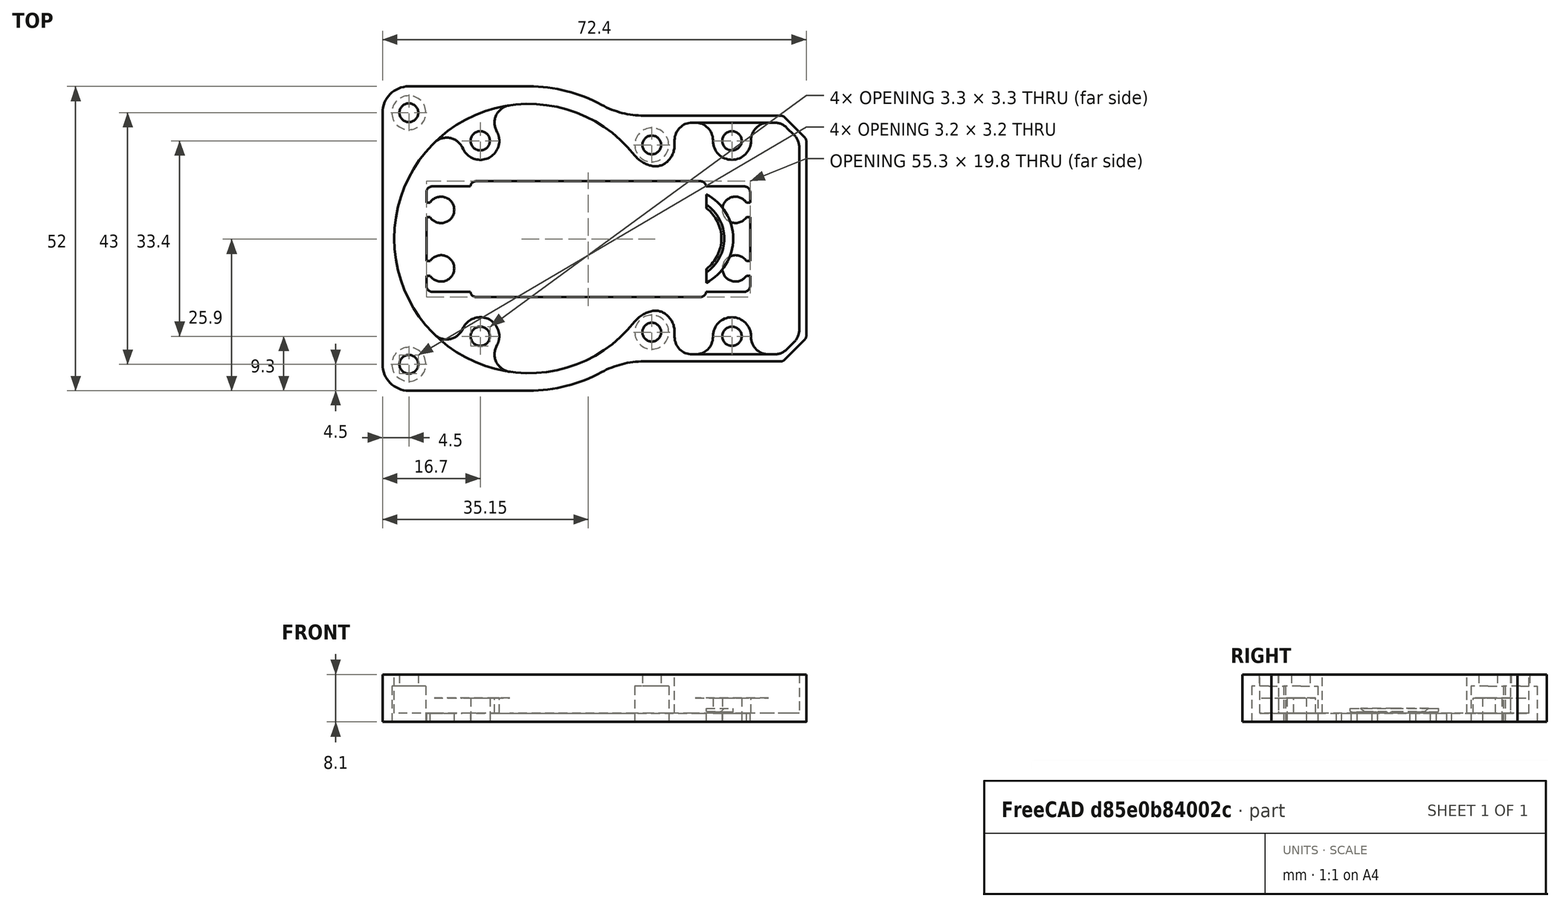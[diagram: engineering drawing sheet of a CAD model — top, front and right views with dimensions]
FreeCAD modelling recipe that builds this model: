
FCSTD DOCUMENT  (FreeCAD 0.18.4R)
Label: motor_part
License: All rights reserved
LicenseURL: http://en.wikipedia.org/wiki/All_rights_reserved
objects: Part::Feature×2, Sketcher::SketchObject×2, Part::FeaturePython×1
note: 5 computed .brp shape members not serialized (recipe doc carries the construction recipe); baked Part::Feature solids carry a one-line shape summary decoded from their .brp

FEATURE [Part::Feature] Part__Feature065  label="motor_support"
  shape: bbox 72.4 x 52 x 8.1 mm, 112 faces (baked)
FEATURE [Part::Feature] Part__Feature006  label="Case"
  Placement = pos=(-10,-10,2) rot=(0.707107,0.707107,0;3.14159rad)
  shape: bbox 68.3 x 20.02 x 42.1 mm, 433 faces (baked)
FEATURE [Part::FeaturePython] Cutout  # WARN: FeaturePython — macro-defined, semantics opaque (R4)
  Base = -> Part__Feature065
  Tolerance = 0
  Tool = -> Part__Feature006
FEATURE [Sketcher::SketchObject] Sketch
  ExternalGeometry = -> [Part__Feature065,Cutout]
  MapMode = 2
  Support = -> [Part__Feature065]
  sketch-geometry (79):
    g0: LineSegment StartX=-20.5 StartY=26 StartZ=0 EndX=-1.07e-14 EndY=26 EndZ=0
    g1: LineSegment StartX=-25 StartY=21.5 StartZ=0 EndX=-25 EndY=-21.5 EndZ=0
    g2: ArcOfCircle CenterX=-20.5 CenterY=-21.5 CenterZ=0 NormalX=0 NormalY=0 NormalZ=1 AngleXU=0 Radius=4.5 StartAngle=3.14159 EndAngle=4.71239
    g3: LineSegment StartX=-20.5 StartY=-26 StartZ=0 EndX=0 EndY=-26 EndZ=0
    g4: ArcOfCircle CenterX=2.88e-14 CenterY=-1.284e-13 CenterZ=0 NormalX=0 NormalY=0 NormalZ=1 AngleXU=0 Radius=26 StartAngle=4.71239 EndAngle=5.21142
    g5: ArcOfCircle CenterX=19.6214 CenterY=-36 CenterZ=0 NormalX=0 NormalY=0 NormalZ=1 AngleXU=0 Radius=15 StartAngle=1.5708 EndAngle=2.06982
    g6: LineSegment StartX=19.6214 StartY=-21 StartZ=0 EndX=42.9858 EndY=-21 EndZ=0
    g7: ArcOfCircle CenterX=42.9858 CenterY=-20 CenterZ=0 NormalX=0 NormalY=0 NormalZ=1 AngleXU=0 Radius=1 StartAngle=4.71239 EndAngle=5.49779
    g8: LineSegment StartX=43.6929 StartY=-20.7071 StartZ=0 EndX=47.1071 EndY=-17.2929 EndZ=0
    g9: LineSegment StartX=47.4 StartY=-16.5858 StartZ=0 EndX=47.4 EndY=16.5858 EndZ=0
    g10: ArcOfCircle CenterX=46.4 CenterY=16.5858 CenterZ=0 NormalX=0 NormalY=0 NormalZ=1 AngleXU=0 Radius=1 StartAngle=0 EndAngle=0.785398
    g11: ArcOfCircle CenterX=8.48e-14 CenterY=3.027e-13 CenterZ=0 NormalX=0 NormalY=0 NormalZ=1 AngleXU=0 Radius=26 StartAngle=1.07177 EndAngle=1.5708
    g12: ArcOfCircle CenterX=-20.5 CenterY=21.5 CenterZ=0 NormalX=0 NormalY=0 NormalZ=1 AngleXU=0 Radius=4.5 StartAngle=1.5708 EndAngle=3.14159
    g13: LineSegment StartX=27.9 StartY=19.8 StartZ=0 EndX=41.9574 EndY=19.8 EndZ=0
    g14: ArcOfCircle CenterX=28.45 CenterY=16.8 CenterZ=0 NormalX=0 NormalY=0 NormalZ=1 AngleXU=0 Radius=3 StartAngle=3e-16 EndAngle=1.5708
    g15: LineSegment StartX=31.45 StartY=16.7 StartZ=0 EndX=31.45 EndY=16.8 EndZ=0
    g16: ArcOfCircle CenterX=34.7 CenterY=16.7 CenterZ=0 NormalX=0 NormalY=0 NormalZ=1 AngleXU=0 Radius=3.25 StartAngle=3.14159 EndAngle=6.28319
    g17: LineSegment StartX=37.95 StartY=16.8 StartZ=0 EndX=37.95 EndY=16.7 EndZ=0
    g18: ArcOfCircle CenterX=40.95 CenterY=16.8 CenterZ=0 NormalX=0 NormalY=0 NormalZ=1 AngleXU=0 Radius=3 StartAngle=1.5708 EndAngle=3.14159
    g19: ArcOfCircle CenterX=41.9574 CenterY=16.8 CenterZ=0 NormalX=0 NormalY=0 NormalZ=1 AngleXU=0 Radius=3 StartAngle=0.785398 EndAngle=1.5708
    g20: LineSegment StartX=44.0789 StartY=18.9211 StartZ=0 EndX=45.3213 EndY=17.6787 EndZ=0
    g21: ArcOfCircle CenterX=43.2 CenterY=15.5574 CenterZ=0 NormalX=0 NormalY=0 NormalZ=1 AngleXU=0 Radius=3 StartAngle=0 EndAngle=0.785398
    g22: LineSegment StartX=46.2 StartY=15.5574 StartZ=0 EndX=46.2 EndY=8.9 EndZ=0
    g23: LineSegment StartX=37.95 StartY=-16.8 StartZ=0 EndX=37.95 EndY=-16.7 EndZ=0
    g24: ArcOfCircle CenterX=34.7 CenterY=-16.7 CenterZ=0 NormalX=0 NormalY=0 NormalZ=1 AngleXU=0 Radius=3.25 StartAngle=2e-16 EndAngle=3.14159
    g25: LineSegment StartX=31.45 StartY=-16.8 StartZ=0 EndX=31.45 EndY=-16.7 EndZ=0
    g26: ArcOfCircle CenterX=28.45 CenterY=-16.8 CenterZ=0 NormalX=0 NormalY=0 NormalZ=1 AngleXU=0 Radius=3 StartAngle=4.71239 EndAngle=6.28319
    g27: Circle CenterX=34.7 CenterY=-16.7 CenterZ=0 NormalX=0 NormalY=0 NormalZ=1 AngleXU=0 Radius=1.65
    g28: ArcOfCircle CenterX=40.95 CenterY=-16.8 CenterZ=0 NormalX=0 NormalY=0 NormalZ=1 AngleXU=0 Radius=3 StartAngle=3.14159 EndAngle=4.71239
    g29: LineSegment StartX=41.9574 StartY=-19.8 StartZ=0 EndX=27.9 EndY=-19.8 EndZ=0
    g30: ArcOfCircle CenterX=41.9574 CenterY=-16.8 CenterZ=0 NormalX=0 NormalY=0 NormalZ=1 AngleXU=0 Radius=3 StartAngle=4.71239 EndAngle=5.49779
    g31: LineSegment StartX=44.0787 StartY=-18.9213 StartZ=0 EndX=45.3213 EndY=-17.6787 EndZ=0
    g32: ArcOfCircle CenterX=43.2 CenterY=-15.5574 CenterZ=0 NormalX=0 NormalY=0 NormalZ=1 AngleXU=0 Radius=3 StartAngle=5.49779 EndAngle=6.28319
    g33: Circle CenterX=34.7 CenterY=16.7 CenterZ=0 NormalX=0 NormalY=0 NormalZ=1 AngleXU=0 Radius=1.65
    g34: LineSegment [constr] StartX=31.45 StartY=16.7 StartZ=0 EndX=33.05 EndY=16.7 EndZ=0
    g35: ArcOfCircle CenterX=19.6214 CenterY=36 CenterZ=0 NormalX=0 NormalY=0 NormalZ=1 AngleXU=0 Radius=15 StartAngle=4.21336 EndAngle=4.71239
    g36: LineSegment StartX=19.6214 StartY=21 StartZ=0 EndX=42.9858 EndY=21 EndZ=0
    g37: ArcOfCircle CenterX=42.9858 CenterY=20 CenterZ=0 NormalX=0 NormalY=0 NormalZ=1 AngleXU=0 Radius=1 StartAngle=0.785398 EndAngle=1.5708
    g38: LineSegment StartX=43.6929 StartY=20.7071 StartZ=0 EndX=47.1068 EndY=17.2932 EndZ=0
    g39: LineSegment [constr] StartX=36.35 StartY=16.7 StartZ=0 EndX=37.95 EndY=16.7 EndZ=0
    g40: LineSegment [constr] StartX=31.45 StartY=-16.7 StartZ=0 EndX=33.05 EndY=-16.7 EndZ=0
    g41: ArcOfCircle CenterX=46.4 CenterY=-16.5858 CenterZ=0 NormalX=0 NormalY=0 NormalZ=1 AngleXU=0 Radius=1 StartAngle=5.49779 EndAngle=6.28319
    g42: ArcOfCircle CenterX=-8.3 CenterY=-16.7 CenterZ=0 NormalX=0 NormalY=0 NormalZ=1 AngleXU=0 Radius=3.25 StartAngle=5.82194 EndAngle=6.28319
    g43: ArcOfCircle CenterX=-8.3 CenterY=-16.7 CenterZ=0 NormalX=0 NormalY=0 NormalZ=1 AngleXU=0 Radius=3.25 StartAngle=-1.42e-14 EndAngle=2.68034
    g44: LineSegment StartX=-11.3659 StartY=-15.5665 StartZ=0 EndX=-11.2104 EndY=-15.2535 EndZ=0
    g45: ArcOfCircle CenterX=-14.0524 CenterY=-14.2313 CenterZ=0 NormalX=0 NormalY=0 NormalZ=1 AngleXU=0 Radius=3 StartAngle=3.93332 EndAngle=5.82194
    g46: LineSegment StartX=-5.54518 StartY=-18.4594 StartZ=0 EndX=-5.38963 EndY=-18.1465 EndZ=0
    g47: ArcOfCircle CenterX=-2.85869 CenterY=-19.7946 CenterZ=0 NormalX=0 NormalY=0 NormalZ=1 AngleXU=0 Radius=3 StartAngle=2.68034 EndAngle=4.56896
    g48: Circle CenterX=-8.3 CenterY=-16.7 CenterZ=0 NormalX=0 NormalY=0 NormalZ=1 AngleXU=0 Radius=1.65
    g49: LineSegment [constr] StartX=-11.3659 StartY=-15.5665 StartZ=0 EndX=-9.89959 EndY=-16.2953 EndZ=0
    g50: ArcOfCircle CenterX=-5.349e-13 CenterY=-1.0646e-12 CenterZ=0 NormalX=0 NormalY=0 NormalZ=1 AngleXU=0 Radius=23 StartAngle=3.93332 EndAngle=4.56896
    g51: LineSegment StartX=27.9 StartY=-19.8 StartZ=0 EndX=19.6214 EndY=-19.8 EndZ=0
    g52: LineSegment [constr] StartX=19.6214 StartY=-21 StartZ=0 EndX=19.6214 EndY=-19.8 EndZ=0
    g53: LineSegment [constr] StartX=12.4428 StartY=-22.8293 StartZ=0 EndX=11.5027 EndY=-21.1043 EndZ=0
    g54: ArcOfCircle CenterX=19.6214 CenterY=-45.7194 CenterZ=0 NormalX=0 NormalY=0 NormalZ=1 AngleXU=0 Radius=25.9194 StartAngle=1.5708 EndAngle=1.88939
    g55: ArcOfCircle CenterX=0.153739 CenterY=13.3044 CenterZ=0 NormalX=0 NormalY=0 NormalZ=1 AngleXU=0 Radius=36.232 StartAngle=4.61727 EndAngle=5.03098
    g56: LineSegment [constr] StartX=-5.38963 StartY=-18.1465 StartZ=0 EndX=-6.82243 EndY=-17.4344 EndZ=0
    g57: LineSegment [constr] StartX=-6.65 StartY=-16.7 StartZ=0 EndX=-5.05 EndY=-16.7 EndZ=0
    g58: ArcOfCircle CenterX=1.28979 CenterY=-14.0146 CenterZ=0 NormalX=0 NormalY=0 NormalZ=1 AngleXU=0 Radius=36.974 StartAngle=1.2522 EndAngle=1.66592
    g59: ArcOfCircle CenterX=-0.0432141 CenterY=-0.043072 CenterZ=0 NormalX=0 NormalY=0 NormalZ=1 AngleXU=0 Radius=22.939 StartAngle=1.66592 EndAngle=2.74111
    g60: ArcOfCircle CenterX=20.955 CenterY=45.608 CenterZ=0 NormalX=0 NormalY=0 NormalZ=1 AngleXU=0 Radius=25.808 StartAngle=4.3938 EndAngle=4.71239
    g61: LineSegment StartX=20.955 StartY=19.8 StartZ=0 EndX=27.9 EndY=19.8 EndZ=0
    g62: Circle CenterX=0 CenterY=2.45e-14 CenterZ=0 NormalX=0 NormalY=0 NormalZ=1 AngleXU=0 Radius=5
    g63: Circle CenterX=-14.9671 CenterY=-5.1 CenterZ=0 NormalX=0 NormalY=0 NormalZ=1 AngleXU=0 Radius=1.9
    g64: LineSegment StartX=-10.9671 StartY=-9.1 StartZ=0 EndX=-21.1185 EndY=-9.1 EndZ=0
    g65: LineSegment StartX=-10.9671 StartY=-9.1 StartZ=0 EndX=-10.9671 EndY=8.9 EndZ=0
    g66: LineSegment StartX=-10.9671 StartY=8.9 StartZ=0 EndX=-21.1671 EndY=8.9 EndZ=0
    g67: Circle CenterX=-15 CenterY=4.9 CenterZ=0 NormalX=0 NormalY=0 NormalZ=1 AngleXU=0 Radius=1.9
    g68: LineSegment [constr] StartX=-15 StartY=4.9 StartZ=0 EndX=-15 EndY=8.9 EndZ=0
    g69: LineSegment [constr] StartX=-14.9671 StartY=-5.1 StartZ=0 EndX=-14.9671 EndY=-9.1 EndZ=0
    g70: LineSegment [constr] StartX=-14.9671 StartY=-5.1 StartZ=0 EndX=-10.9671 EndY=-5.1 EndZ=0
    g71: Circle CenterX=35.3 CenterY=4.9 CenterZ=0 NormalX=0 NormalY=0 NormalZ=1 AngleXU=0 Radius=1.9
    g72: Circle CenterX=35.3 CenterY=-5.1 CenterZ=0 NormalX=0 NormalY=0 NormalZ=1 AngleXU=0 Radius=1.9
    g73: LineSegment [constr] StartX=35.3 StartY=-5.1 StartZ=0 EndX=35.3 EndY=-9.1 EndZ=0
    g74: LineSegment StartX=31.3 StartY=-9.1 StartZ=0 EndX=31.3 EndY=8.9 EndZ=0
    g75: LineSegment StartX=31.3 StartY=8.9 StartZ=0 EndX=46.2 EndY=8.9 EndZ=0
    g76: LineSegment StartX=31.3 StartY=-9.1 StartZ=0 EndX=46.2 EndY=-9.1 EndZ=0
    g77: ArcOfCircle CenterX=-0.0432141 CenterY=-0.043072 CenterZ=0 NormalX=0 NormalY=0 NormalZ=1 AngleXU=0 Radius=22.939 StartAngle=3.54747 EndAngle=3.93334
    g78: LineSegment StartX=46.2 StartY=-9.1 StartZ=0 EndX=46.2 EndY=-15.5574 EndZ=0
  constraints (189):
    c: Coincident(g0,g-4)
    c: Coincident(g0,g-20)
    c: Coincident(g2,g-7)
    c: Coincident(g3,g-8)
    c: Coincident(g4,g3)
    c: Coincident(g4,g-9)
    c: Coincident(g5,g-10)
    c: Coincident(g6,g-11)
    c: Coincident(g7,g-12)
    c: Coincident(g8,g-13)
    c: Coincident(g9,g-15)
    c: Coincident(g10,g-16)
    c: Coincident(g11,g0)
    c: Coincident(g11,g-20) = 1.5708
    c: Tangent(g12,g0) = 1.5708
    c: Tangent(g12,g1) = -1.5708
    c: Tangent(g2,g1) = -1.5708
    c: Tangent(g3,g2) = -1.5708
    c: Radius(g12) = 4.5
    c: Angle(g2) = 1.5708
    c: Tangent(g8,g7) = -1.5708
    c: Coincident(g9,g-14) = -1.5708
    c: Coincident(g13,g-26)
    c: Coincident(g13,g-27)
    c: Coincident(g14,g-21)
    c: Coincident(g14,g-23)
    c: Coincident(g15,g-23)
    c: Tangent(g15,g14) = -1.5708
    c: Coincident(g16,g-24)
    c: Tangent(g16,g15) = 1.5708
    c: Coincident(g17,g-25)
    c: Coincident(g18,g-25)
    c: Tangent(g18,g17) = -1.5708
    c: Coincident(g19,g-28)
    c: Tangent(g19,g13) = 1.5708
    c: Coincident(g20,g-29)
    c: Coincident(g21,g-30)
    c: Tangent(g21,g20) = 1.5708
    c: Tangent(g22,g21) = 1.5708
    c: Coincident(g23,g-37)
    c: Coincident(g23,g-36) = 1.5708
    c: Coincident(g24,g-38)
    c: Tangent(g24,g23) = -1.5708
    c: Coincident(g25,g-39)
    c: Coincident(g26,g-39)
    c: Tangent(g26,g25) = -1.5708
    c: PointOnObject(g-41,g27)
    c: PointOnObject(g-41,g27)
    c: Tangent(g27,g-40)
    c: Coincident(g28,g23)
    c: Coincident(g28,g-35)
    c: Tangent(g28,g-35)
    c: Coincident(g29,g-34)
    c: Coincident(g29,g-34)
    c: Coincident(g30,g29)
    c: Coincident(g30,g-33)
    c: Tangent(g30,g-33)
    c: Coincident(g31,g30)
    c: Coincident(g31,g-32)
    c: PointOnObject(g-43,g33)
    c: PointOnObject(g-43,g33)
    c: Radius(g18) = 3
    c: Coincident(g34,g15)
    c: Coincident(g34,g-43)
    c: Perpendicular(g33,g34)
    c: Distance(g20) = 1.757
    c: Coincident(g35,g-19)
    c: Coincident(g36,g-18)
    c: Coincident(g37,g-17)
    c: Tangent(g35,g11) = 1.5708
    c: Tangent(g36,g35) = -1.5708
    c: Coincident(g39,g-43)
    c: Coincident(g39,g16)
    c: Equal(g17,g15)
    c: Tangent(g10,g9) = -1.5708
    c: Tangent(g7,g6)
    c: Coincident(g40,g24)
    c: Coincident(g40,g-41)
    c: Perpendicular(g25,g40)
    c: DistanceY(g25,g25) = 0.1
    c: Angle(g7) = 0.785398
    c: Tangent(g37,g36) = 1.5708
    c: Tangent(g38,g37) = 1.5708
    c: Tangent(g32,g31) = -1.5708
    c: Tangent(g41,g9) = -1.5708
    c: Tangent(g41,g8)
    c: Tangent(g6,g5) = 1.5708
    c: Tangent(g5,g4) = 1.5708
    c: Distance(g38) = 4.828
    c: Angle(g41) = 0.785398
    c: Coincident(g42,g-46)
    c: Coincident(g43,g-48)
    c: Coincident(g44,g-49)
    c: Coincident(g45,g-49)
    c: Coincident(g46,g-45)
    c: Coincident(g47,g46)
    c: Coincident(g47,g-44)
    c: Tangent(g47,g-44)
    c: PointOnObject(g-51,g48)
    c: PointOnObject(g-51,g48)
    c: Tangent(g45,g44) = -1.5708
    c: Tangent(g44,g43) = 1.5708
    c: Coincident(g49,g44)
    c: PointOnObject(g49,g48)
    c: Perpendicular(g44,g49)
    c: Tangent(g46,g42) = -1.5708
    c: Tangent(g43,g42) = -1.5708
    c: Coincident(g50,g47)
    c: Tangent(g50,g45) = -1.5708
    c: Coincident(g51,g29)
    c: Horizontal(g51)
    c: Coincident(g52,g5)
    c: Coincident(g52,g51)
    c: Perpendicular(g51,g52)
    c: Coincident(g53,g4)
    c: Perpendicular(g5,g53)
    c: Coincident(g54,g53)
    c: Tangent(g54,g51) = -1.5708
    c: Tangent(g55,g54) = 1.5708
    c: Angle(g54) = 0.318592
    c: Angle(g55) = 0.413713
    c: Radius(g55) = 36.232
    c: Coincident(g56,g42)
    c: PointOnObject(g56,g48)
    c: Perpendicular(g48,g56)
    c: Perpendicular(g46,g56)
    c: Coincident(g57,g-51)
    c: Coincident(g57,g42)
    c: Horizontal(g57)
    c: Angle(g58) = 0.413713
    c: Tangent(g59,g58) = -1.5708
    c: Coincident(g77,g45) = -1.5708
    c: Angle(g60) = 0.318592
    c: Tangent(g60,g58) = 1.5708
    c: Coincident(g61,g13)
    c: Horizontal(g61)
    c: Tangent(g61,g60) = -1.5708
    c: Radius(g58) = 36.974
    c: Radius(g60) = 25.808
    c: PointOnObject(g-53,g62)
    c: PointOnObject(g-53,g62)
    c: Tangent(g62,g-52)
    c: Radius(g63) = 1.9
    c: PointOnObject(g64,g-66)
    c: Horizontal(g64)
    c: Coincident(g65,g64)
    c: PointOnObject(g65,g-54)
    c: Vertical(g65)
    c: Coincident(g66,g65)
    c: Horizontal(g66)
    c: Coincident(g67,g-58)
    c: Radius(g67) = 1.9
    c: DistanceY(g63,g67) = 10
    c: Coincident(g68,g67)
    c: PointOnObject(g68,g66)
    c: Vertical(g68)
    c: Coincident(g69,g63)
    c: PointOnObject(g69,g64)
    c: Vertical(g69)
    c: Coincident(g70,g63)
    c: PointOnObject(g70,g65)
    c: Horizontal(g70)
    c: DistanceX(g70,g70) = 4
    c: Coincident(g71,g-78)
    c: Coincident(g72,g-79)
    c: Radius(g71) = 1.9
    c: Radius(g72) = 1.9
    c: Coincident(g73,g72)
    c: PointOnObject(g73,g-67)
    c: Vertical(g73)
    c: PointOnObject(g74,g-67)
    c: PointOnObject(g74,g-77)
    c: Vertical(g74)
    c: DistanceX(g74,g73) = 4
    c: Coincident(g75,g74)
    c: Horizontal(g75)
    c: Perpendicular(g22,g75)
    c: Coincident(g76,g74)
    c: Horizontal(g76)
    c: Equal(g59,g77)
    c: Coincident(g59,g66)
    c: Coincident(g77,g64)
    c: Coincident(g59,g77)
    c: Angle(g59) = 1.07519
    c: DistanceX(g66,g66) = 10.2
    c: Coincident(g22,g75)
    c: Coincident(g78,g76)
    c: Tangent(g22,g78)
    c: Tangent(g32,g78) = 1.5708
FEATURE [Sketcher::SketchObject] Sketch001
  ExternalGeometry = -> [Part__Feature065]
  MapMode = 4
  Placement = pos=(0,0,0) rot=(0.57735,0.57735,0.57735;2.0944rad)
  Support = -> [Part__Feature065]
  sketch-geometry (7):
    g0: LineSegment StartX=-26 StartY=6.9 StartZ=0 EndX=26 EndY=6.9 EndZ=0
    g1: LineSegment StartX=26 StartY=6.9 StartZ=0 EndX=26 EndY=-1.2 EndZ=0
    g2: LineSegment StartX=26 StartY=-1.2 StartZ=0 EndX=-26 EndY=-1.2 EndZ=0
    g3: LineSegment StartX=-26 StartY=-1.2 StartZ=0 EndX=-26 EndY=6.9 EndZ=0
    g4: LineSegment StartX=16.7 StartY=0.3 StartZ=0 EndX=16.7 EndY=2.9 EndZ=0
    g5: LineSegment StartX=-16.7 StartY=0.3 StartZ=0 EndX=-16.7 EndY=-1.2 EndZ=0
    g6: LineSegment StartX=-16.7 StartY=2.9 StartZ=0 EndX=-16.7 EndY=0.3 EndZ=0
  constraints (15):
    c: Coincident(g0,g-5)
    c: Coincident(g0,g-8)
    c: Coincident(g1,g0)
    c: Coincident(g1,g-8)
    c: Coincident(g2,g1)
    c: Coincident(g2,g-5)
    c: Coincident(g3,g2)
    c: Coincident(g3,g0)
    c: Coincident(g4,g-13)
    c: Coincident(g4,g-12)
    c: Coincident(g5,g-14)
    c: PointOnObject(g5,g2)
    c: Vertical(g5)
    c: Coincident(g6,g-15)
    c: Coincident(g6,g5)
